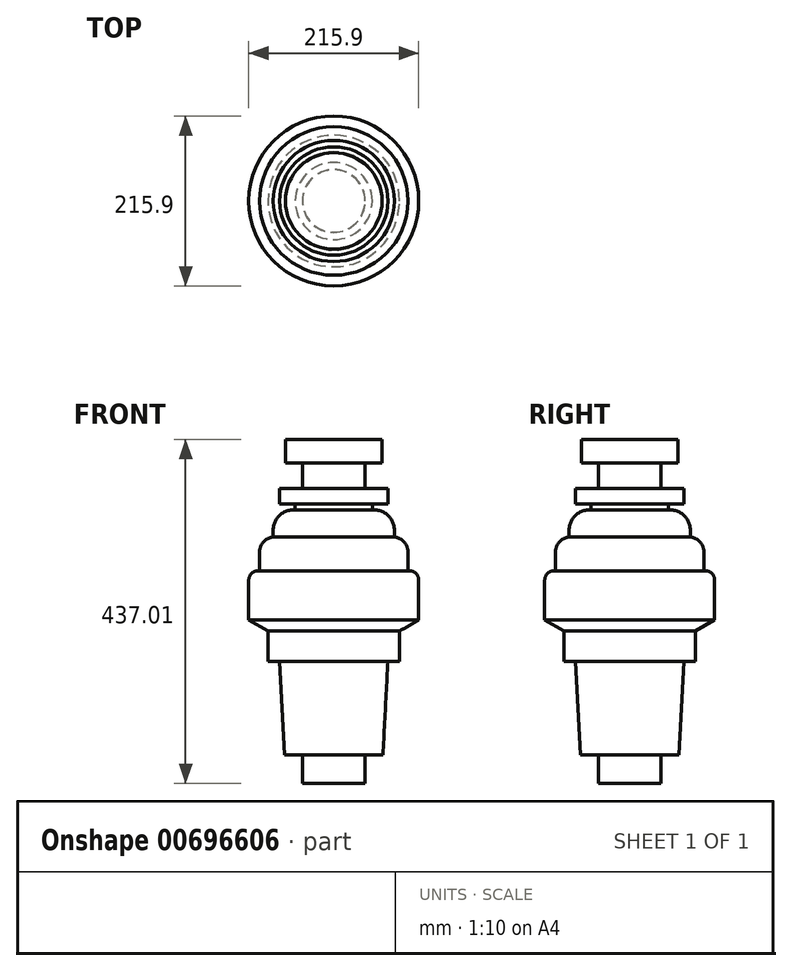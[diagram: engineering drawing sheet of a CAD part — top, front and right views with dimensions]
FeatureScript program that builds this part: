
annotation { "Feature Type Name" : "Feature", "Feature Type Description" : "" }
export const myFeature = defineFeature(function(context is Context, id is Id, definition is map)
    precondition{}
    {
        {
            var Q0;
            Q0=qCreatedBy(makeId("Front.planeOp"),FACE);
            var sketch = newSketch(context, id + "F0", { "sketchPlane" : qUnion([Q0])});
            skLineSegment(sketch, "E0", {"start": v(0, 437.01) * mm, "end": v(0, 0) * mm});
            skLineSegment(sketch, "E1", {"start": v(0, 0) * mm, "end": v(-39.69, 0) * mm});
            skLineSegment(sketch, "E2", {"start": v(-39.69, 0) * mm, "end": v(-39.69, 36.06) * mm});
            skLineSegment(sketch, "E3", {"start": v(-39.69, 36.06) * mm, "end": v(-62.4, 36.06) * mm});
            skLineSegment(sketch, "E4", {"start": v(-62.4, 36.06) * mm, "end": v(-68.74, 154.86) * mm});
            skLineSegment(sketch, "E5", {"start": v(-68.74, 154.86) * mm, "end": v(-83.56, 154.86) * mm});
            skLineSegment(sketch, "E6", {"start": v(-83.56, 154.86) * mm, "end": v(-83.56, 193.57) * mm});
            skLineSegment(sketch, "E7", {"start": v(-83.56, 193.57) * mm, "end": v(-107.95, 207.58) * mm});
            skLineSegment(sketch, "E8", {"start": v(-107.95, 207.58) * mm, "end": v(-107.95, 270.18) * mm});
            skLineSegment(sketch, "E9", {"start": v(-107.95, 270.18) * mm, "end": v(-94.27, 270.18) * mm});
            skLineSegment(sketch, "E10", {"start": v(-94.27, 270.18) * mm, "end": v(-94.27, 313) * mm});
            skLineSegment(sketch, "E11", {"start": v(-94.27, 313) * mm, "end": v(-76.97, 313) * mm});
            skLineSegment(sketch, "E12", {"start": v(-76.97, 313) * mm, "end": v(-76.97, 347.6) * mm});
            skLineSegment(sketch, "E13", {"start": v(-76.97, 347.6) * mm, "end": v(-48.97, 347.6) * mm});
            skLineSegment(sketch, "E14", {"start": v(-48.97, 347.6) * mm, "end": v(-48.97, 355.01) * mm});
            skLineSegment(sketch, "E15", {"start": v(-48.97, 355.01) * mm, "end": v(-68.74, 355.01) * mm});
            skLineSegment(sketch, "E16", {"start": v(-68.74, 355.01) * mm, "end": v(-68.74, 374.78) * mm});
            skLineSegment(sketch, "E17", {"start": v(-68.74, 374.78) * mm, "end": v(-39.9, 374.78) * mm});
            skLineSegment(sketch, "E18", {"start": v(-39.9, 374.78) * mm, "end": v(-39.9, 406.9) * mm});
            skLineSegment(sketch, "E19", {"start": v(-39.9, 406.9) * mm, "end": v(-61.33, 406.9) * mm});
            skLineSegment(sketch, "E20", {"start": v(-61.33, 406.9) * mm, "end": v(-61.33, 437.01) * mm});
            skLineSegment(sketch, "E21", {"start": v(-61.33, 437.01) * mm, "end": v(0, 437.01) * mm});
            skSolve(sketch);
        }
        {
            var Q0;
            Q0 = qSketchRegion(id + "F0", true);
            var Q1;
            Q1=sQuery(id+"F0.wireOp",EDGE,"E0");
            revolve(context, id + "F1", {"entities" : qUnion([Q0]), "axis" : qUnion([Q1]), "revolveType" : RevolveType.FULL});
        }
        {
            var Q0;
            Q0=makeQuery(id+"F1.opRevolve","SWEPT_EDGE",EDGE,{"disambiguationData":[OSD([sQuery(id+"F0.wireOp",EDGE,"E12"),sQuery(id+"F0.wireOp",EDGE,"E13")])]});
            fillet(context, id + "F2", {"entities" : qUnion([Q0]), "radius" : 25.75 * mm, "tangentPropagation" : true, "allowEdgeOverflow" : false});
        }
        {
            var Q0;
            Q0=makeQuery(id+"F1.opRevolve","SWEPT_EDGE",EDGE,{"disambiguationData":[OSD([sQuery(id+"F0.wireOp",EDGE,"E10"),sQuery(id+"F0.wireOp",EDGE,"E11")])]});
            fillet(context, id + "F3", {"entities" : qUnion([Q0]), "radius" : 19 * mm, "tangentPropagation" : true, "allowEdgeOverflow" : false});
        }
        {
            var Q0;
            Q0=makeQuery(id+"F1.opRevolve","SWEPT_EDGE",EDGE,{"disambiguationData":[OSD([sQuery(id+"F0.wireOp",EDGE,"E8"),sQuery(id+"F0.wireOp",EDGE,"E9")])]});
            fillet(context, id + "F4", {"entities" : qUnion([Q0]), "radius" : 11.65 * mm, "tangentPropagation" : true, "allowEdgeOverflow" : false});
        }
    });
